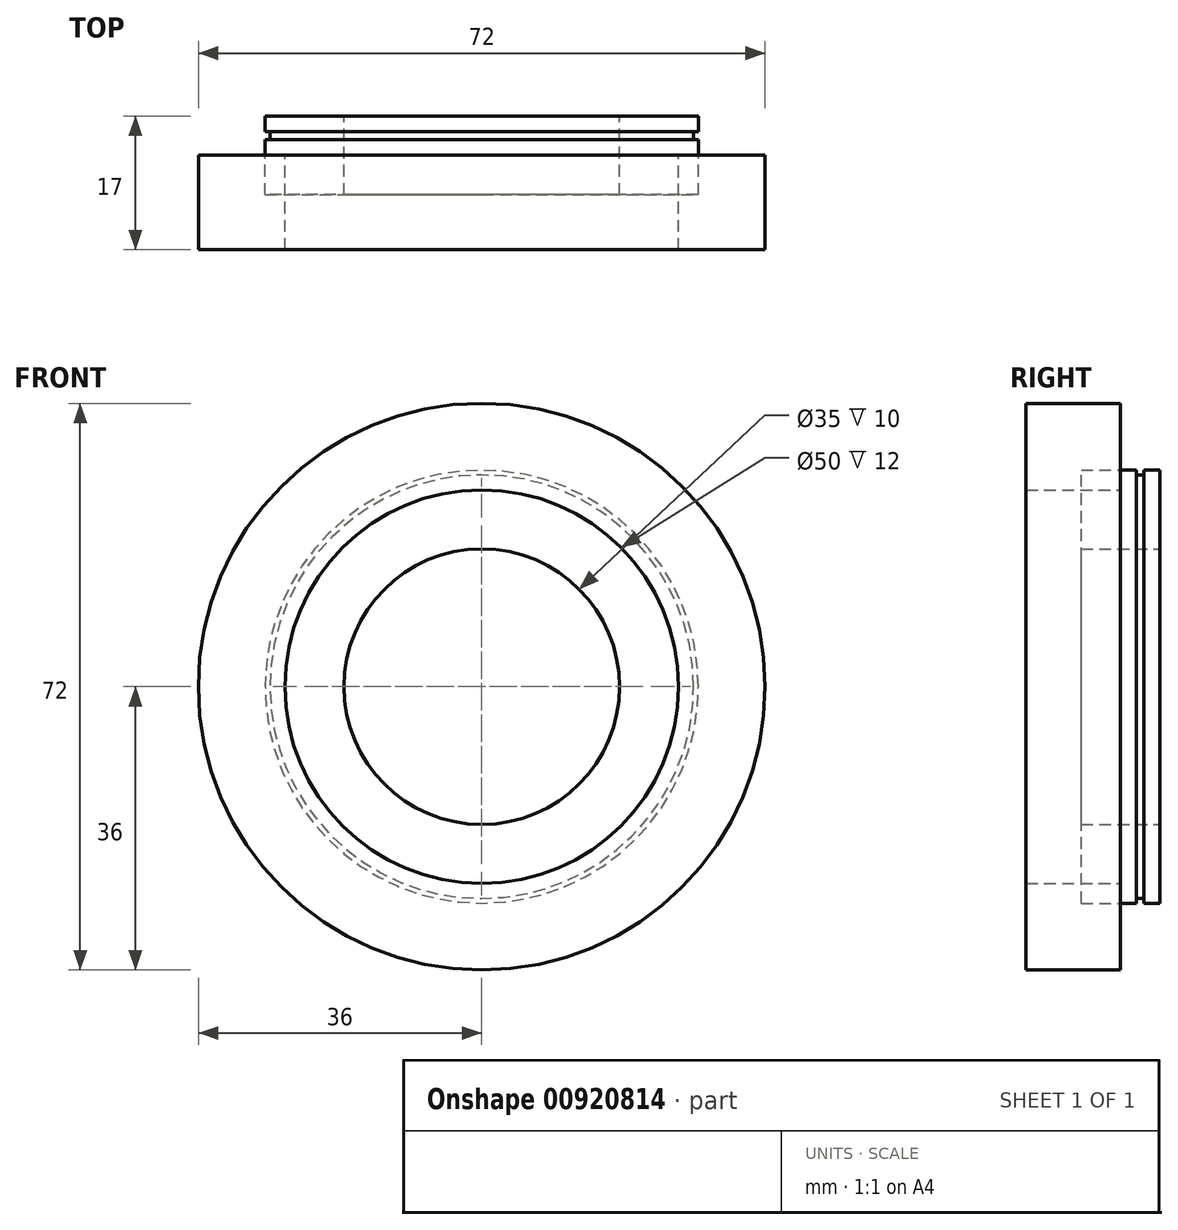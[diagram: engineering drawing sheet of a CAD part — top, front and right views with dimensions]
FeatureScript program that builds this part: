
annotation { "Feature Type Name" : "Feature", "Feature Type Description" : "" }
export const myFeature = defineFeature(function(context is Context, id is Id, definition is map)
    precondition{}
    {
        {
            var Q0;
            Q0=qCreatedBy(makeId("Front.planeOp"),FACE);
            var sketch = newSketch(context, id + "F0", { "sketchPlane" : qUnion([Q0])});
            skCircle(sketch, "E0", {"center": v(0, 0) * mm, "radius": 17.5 * mm});
            skCircle(sketch, "E1", {"center": v(0, 0) * mm, "radius": 27.5 * mm});
            skSolve(sketch);
        }
        {
            var Q0;
            Q0 = qSketchRegion(id + "F0", true);
            extrude(context, id + "F1", {"entities" : qUnion([Q0]), "endBound" : BoundingType.SYMMETRIC, "depth" : 10 * mm, "offsetDistance" : 25 * mm});
        }
        {
            var Q0;
            Q0=makeQuery(id+"F1.opExtrude","CAP_FACE",FACE,{"disambiguationData":[OSD([sQuery(id+"F0.wireOp",EDGE,"E0"),sQuery(id+"F0.wireOp",EDGE,"E1")])],"isStart":false});
            cPlane(context, id + "F2", {"entities" : qUnion([Q0]), "cplaneType" : CPlaneType.OFFSET, "offset" : 7 * mm, "oppositeDirection" : true, "width" : 150 * mm, "height" : 150 * mm});
        }
        {
            var Q0;
            Q0=qCreatedBy(id+"F2.planeOp",FACE);
            var sketch = newSketch(context, id + "F3", { "sketchPlane" : qUnion([Q0])});
            skCircle(sketch, "E2", {"center": v(0, 0) * mm, "radius": 26.9 * mm});
            skCircle(sketch, "E3.0", {"center": v(0, 0) * mm, "radius": 27.5 * mm});
            skSolve(sketch);
        }
        {
            var Q0;
            Q0 = qSketchRegion(id + "F3", true);
            extrude(context, id + "F4", {"entities" : qUnion([Q0]), "operationType" : NewBodyOperationType.REMOVE, "oppositeDirection" : true, "depth" : 1 * mm, "offsetDistance" : 25 * mm});
        }
        {
            var Q0;
            Q0=qCreatedBy(makeId("Front.planeOp"),FACE);
            var sketch = newSketch(context, id + "F5", { "sketchPlane" : qUnion([Q0])});
            skCircle(sketch, "E4", {"center": v(0, 0) * mm, "radius": 25 * mm});
            skCircle(sketch, "E5", {"center": v(0, 0) * mm, "radius": 36 * mm});
            skSolve(sketch);
        }
        {
            var Q0;
            Q0 = qSketchRegion(id + "F5", true);
            extrude(context, id + "F6", {"entities" : qUnion([Q0]), "depth" : 12 * mm, "offsetDistance" : 25 * mm});
        }
    });
